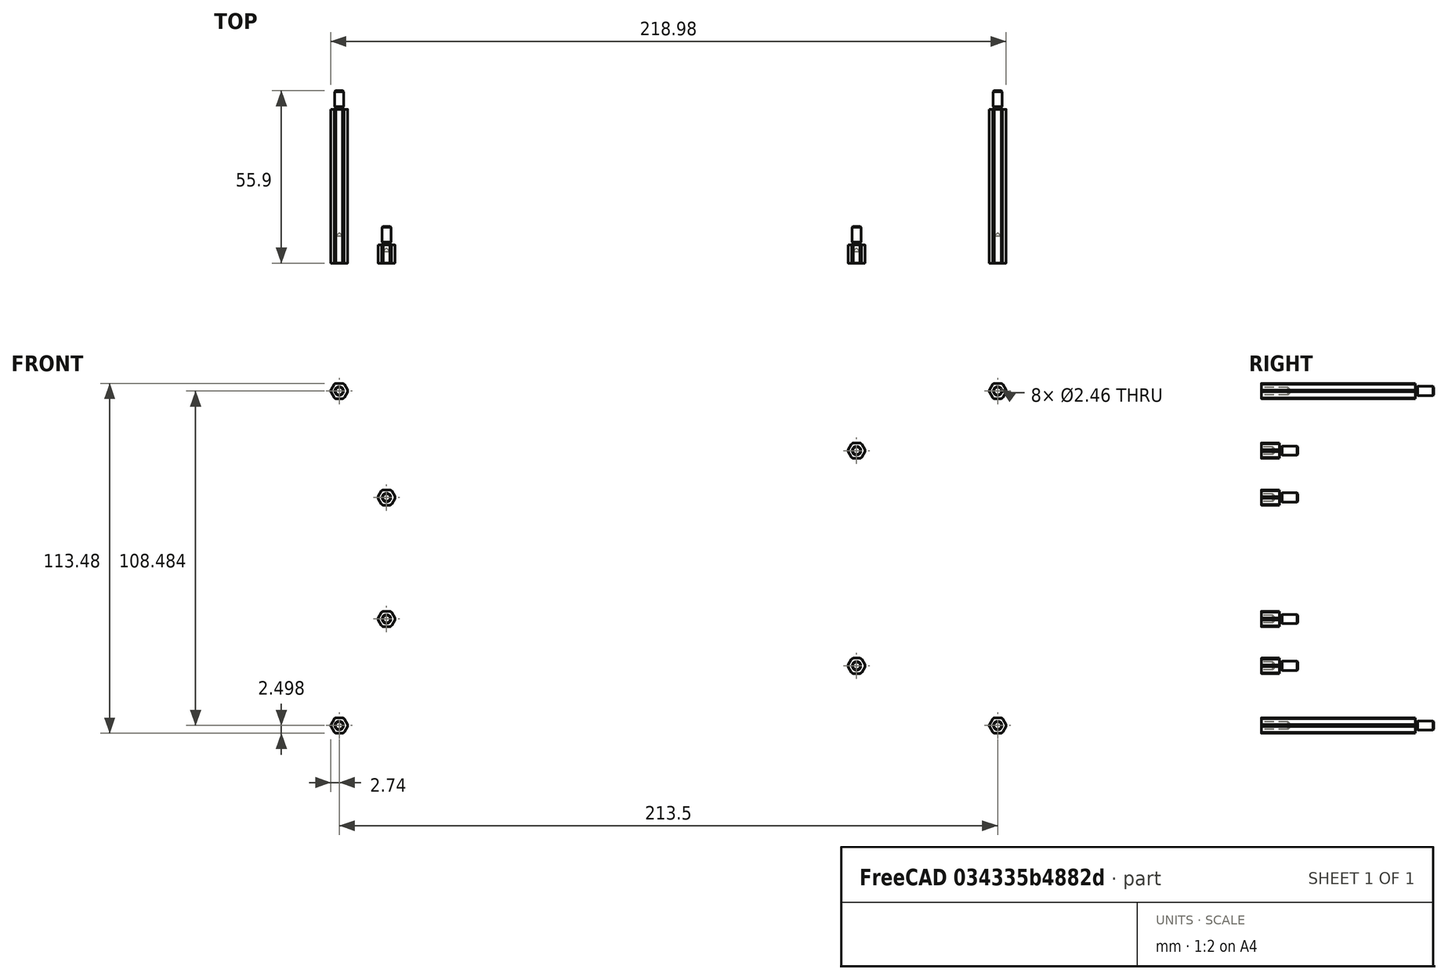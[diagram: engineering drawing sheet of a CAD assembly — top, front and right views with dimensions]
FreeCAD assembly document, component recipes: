
FREECAD ASSEMBLY — COMPONENT RECIPES ("psu")

This assembly document has 8 components, labeled P0..P7 below (a component is one placed body or linked part). 7 of them carry a construction recipe — the FreeCAD feature program that regenerates the part from scratch, quoted from this document or its linked companion documents; the rest are supplied as boundary geometry only. No exploded tour is included for this assembly.
COMPONENT P0 — recipe-attached ("PowerEntry", a linked part whose construction recipe lives in a companion FreeCAD document of the same project; that document's serialized recipe follows).
Construction recipe (the companion document, serialized — sketch geometry with constraints, then the solid features built on it; lengths are millimeters unless a unit is written):

FCSTD DOCUMENT  (FreeCAD 1.0R38641 +468 (Git))
Label: qualtek_power_entry
License: All rights reserved
LicenseURL: https://en.wikipedia.org/wiki/All_rights_reserved
objects: Sketcher::SketchObject×2, PartDesign::Pad×1, PartDesign::Pocket×1, PartDesign::Body×1
note: 11 computed .brp shape members not serialized (recipe doc carries the construction recipe); baked Part::Feature solids carry a one-line shape summary decoded from their .brp

FEATURE [Sketcher::SketchObject] Sketch001
  ArcFitTolerance = 1e-06
  FullyConstrained = false
  MakeInternals = false
  MapMode = 5
  Placement = pos=(0,0,0) rot=(0.57735,0.57735,0.57735;2.0944rad)
  sketch-geometry (17):
    g0: LineSegment StartX=39 StartY=9.70127 StartZ=0 EndX=39 EndY=40.2987 EndZ=0
    g1: LineSegment StartX=-39 StartY=40.2987 StartZ=0 EndX=-39 EndY=9.70127 EndZ=0
    g2: LineSegment StartX=36.545 StartY=43.2488 StartZ=0 EndX=0 EndY=50 EndZ=0
    g3: LineSegment StartX=0 StartY=50 StartZ=0 EndX=-36.545 EndY=43.2488 EndZ=0
    g4: LineSegment StartX=-36.545 StartY=6.75119 StartZ=0 EndX=0 EndY=0 EndZ=0
    g5: LineSegment StartX=0 StartY=0 StartZ=0 EndX=36.545 EndY=6.75119 EndZ=0
    g6: ArcOfCircle CenterX=-36 CenterY=40.2987 CenterZ=0 NormalX=0 NormalY=0 NormalZ=1 AngleXU=0 Radius=3 StartAngle=1.75347 EndAngle=3.14159
    g7: GeomPoint [constr] X=-39 Y=42.7953 Z=0
    g8: ArcOfCircle CenterX=36 CenterY=40.2987 CenterZ=0 NormalX=0 NormalY=0 NormalZ=1 AngleXU=0 Radius=3 StartAngle=7e-16 EndAngle=1.38812
    g9: GeomPoint [constr] X=39 Y=42.7953 Z=0
    g10: ArcOfCircle CenterX=36 CenterY=9.70127 CenterZ=0 NormalX=0 NormalY=0 NormalZ=1 AngleXU=0 Radius=3 StartAngle=4.89507 EndAngle=6.28319
    g11: GeomPoint [constr] X=39 Y=7.20472 Z=0
    g12: ArcOfCircle CenterX=-36 CenterY=9.70127 CenterZ=0 NormalX=0 NormalY=0 NormalZ=1 AngleXU=0 Radius=3 StartAngle=3.14159 EndAngle=4.52971
    g13: GeomPoint [constr] X=-39 Y=7.20472 Z=0
    g14: LineSegment [constr] StartX=-39 StartY=25 StartZ=0 EndX=39 EndY=25 EndZ=0
    g15: LineSegment [constr] StartX=0 StartY=50 StartZ=0 EndX=2.5e-15 EndY=25 EndZ=0
    g16: LineSegment [constr] StartX=2.5e-15 StartY=25 StartZ=0 EndX=0 EndY=0 EndZ=0
  constraints (38):
    c: Vertical(g0)
    c: Vertical(g1)
    c: Coincident(g2,g3)
    c: Coincident(g4,g5)
    c: DistanceY(g4,g2) = 50
    c: DistanceX(g13,g11) = 78
    c: PointOnObject(g7,g1)
    c: PointOnObject(g7,g3)
    c: Tangent(g1,g6) = -1.5708
    c: Tangent(g3,g6) = -1.5708
    c: PointOnObject(g9,g0)
    c: PointOnObject(g9,g2)
    c: Tangent(g0,g8) = -1.5708
    c: Tangent(g2,g8) = -1.5708
    c: PointOnObject(g11,g0)
    c: PointOnObject(g11,g5)
    c: Tangent(g0,g10) = -1.5708
    c: Tangent(g5,g10) = -1.5708
    c: PointOnObject(g13,g1)
    c: PointOnObject(g13,g4)
    c: Tangent(g1,g12) = -1.5708
    c: Tangent(g4,g12) = -1.5708
    c: Equal(g12,g6)
    c: Equal(g6,g8)
    c: Equal(g8,g10)
    c: Radius(g6) = 3
    c: Equal(g3,g2)
    c: Coincident(g4,g-1)
    c: Equal(g0,g1)
    c: Equal(g5,g4)
    c: PointOnObject(g2,g-2)
    c: Symmetric(g1,g1,g14)
    c: Symmetric(g0,g0,g14)
    c: Coincident(g15,g2)
    c: Symmetric(g14,g14,g15)
    c: Coincident(g16,g15)
    c: Coincident(g16,g4)
    c: Equal(g16,g15)
FEATURE [Sketcher::SketchObject] Sketch
  ArcFitTolerance = 1e-06
  AttachmentSupport = -> [YZ_Plane]
  ExternalGeometry = -> [Sketch001]
  FullyConstrained = true
  MakeInternals = false
  MapMode = 5
  Placement = pos=(0,0,0) rot=(0.57735,0.57735,0.57735;2.0944rad)
  sketch-geometry (18):
    g0: LineSegment StartX=-33.75 StartY=10.95 StartZ=0 EndX=33.75 EndY=10.95 EndZ=0
    g1: LineSegment StartX=36.25 StartY=13.45 StartZ=0 EndX=36.25 EndY=36.55 EndZ=0
    g2: LineSegment StartX=33.75 StartY=39.05 StartZ=0 EndX=-33.75 EndY=39.05 EndZ=0
    g3: LineSegment StartX=-36.25 StartY=36.55 StartZ=0 EndX=-36.25 EndY=13.45 EndZ=0
    g4: Circle CenterX=0 CenterY=45 CenterZ=0 NormalX=0 NormalY=0 NormalZ=1 AngleXU=0 Radius=1.75
    g5: Circle CenterX=-1.13e-14 CenterY=5 CenterZ=0 NormalX=0 NormalY=0 NormalZ=1 AngleXU=0 Radius=1.75
    g6: ArcOfCircle CenterX=-33.75 CenterY=36.55 CenterZ=0 NormalX=0 NormalY=0 NormalZ=1 AngleXU=0 Radius=2.5 StartAngle=1.5708 EndAngle=3.14159
    g7: GeomPoint [constr] X=-36.25 Y=39.05 Z=0
    g8: ArcOfCircle CenterX=-33.75 CenterY=13.45 CenterZ=0 NormalX=0 NormalY=0 NormalZ=1 AngleXU=0 Radius=2.5 StartAngle=3.14159 EndAngle=4.71239
    g9: GeomPoint [constr] X=-36.25 Y=10.95 Z=0
    g10: ArcOfCircle CenterX=33.75 CenterY=13.45 CenterZ=0 NormalX=0 NormalY=0 NormalZ=1 AngleXU=0 Radius=2.5 StartAngle=4.71239 EndAngle=6.28319
    g11: GeomPoint [constr] X=36.25 Y=10.95 Z=0
    g12: ArcOfCircle CenterX=33.75 CenterY=36.55 CenterZ=0 NormalX=0 NormalY=0 NormalZ=1 AngleXU=0 Radius=2.5 StartAngle=8e-16 EndAngle=1.5708
    g13: GeomPoint [constr] X=36.25 Y=39.05 Z=0
    g14: LineSegment [constr] StartX=0 StartY=45 StartZ=0 EndX=0 EndY=39.05 EndZ=0
    g15: LineSegment [constr] StartX=-1.13e-14 StartY=5 StartZ=0 EndX=-1.13e-14 EndY=10.95 EndZ=0
    g16: LineSegment [constr] StartX=0 StartY=50 StartZ=0 EndX=0 EndY=45 EndZ=0
    g17: LineSegment [constr] StartX=-1.13e-14 StartY=5 StartZ=0 EndX=0 EndY=0 EndZ=0
  constraints (42):
    c: Horizontal(g0)
    c: Horizontal(g2)
    c: Vertical(g1)
    c: Vertical(g3)
    c: Diameter(g4) = 3.5
    c: DistanceY(g5,g4) = 40
    c: DistanceY(g11,g13) = 28.1
    c: DistanceX(g9,g11) = 72.5
    c: PointOnObject(g7,g2)
    c: PointOnObject(g7,g3)
    c: Tangent(g2,g6) = -1.5708
    c: Tangent(g3,g6) = -1.5708
    c: PointOnObject(g9,g0)
    c: PointOnObject(g9,g3)
    c: Tangent(g0,g8) = -1.5708
    c: Tangent(g3,g8) = -1.5708
    c: PointOnObject(g11,g0)
    c: PointOnObject(g11,g1)
    c: Tangent(g0,g10) = -1.5708
    c: Tangent(g1,g10) = -1.5708
    c: PointOnObject(g13,g1)
    c: PointOnObject(g13,g2)
    c: Tangent(g1,g12) = -1.5708
    c: Tangent(g2,g12) = -1.5708
    c: Equal(g8,g6)
    c: Equal(g12,g10)
    c: Equal(g8,g10)
    c: Radius(g8) = 2.5
    c: Coincident(g14,g4)
    c: Symmetric(g2,g2,g14)
    c: Vertical(g14)
    c: Coincident(g15,g5)
    c: Symmetric(g0,g0,g15)
    c: Vertical(g15)
    c: Equal(g15,g14)
    c: Equal(g5,g4)
    c: Coincident(g16,g-3)
    c: Coincident(g16,g4)
    c: Vertical(g16)
    c: Coincident(g17,g5)
    c: Coincident(g17,g-1)
    c: Equal(g17,g16)
FEATURE [PartDesign::Pad] Pad
  Direction = (1,0,0)
  Length = 5
  Length2 = 10
  Placement = pos=(0,0,0) rot=(0.57735,0.57735,0.57735;2.0944rad)
  Profile = -> Sketch001
  ReferenceAxis = -> Sketch001 [N_Axis]
  Refine = true
  Suppressed = false
  Type = 0
FEATURE [PartDesign::Pocket] Pocket
  BaseFeature = -> Pad
  Direction = (-1,0,0)
  Length = 0
  Length2 = 5
  Placement = pos=(0,0,0) rot=(0.57735,0.57735,0.57735;2.0944rad)
  Profile = -> Sketch
  ReferenceAxis = -> Sketch [N_Axis]
  Refine = true
  Suppressed = false
  Type = 3
  UpToFace = -> Pad [Face12]
FEATURE [PartDesign::Body] Body  label="PowerEntry"
  AllowCompound = false
  Group = -> [Sketch001,Pad,Sketch,Pocket]
  Origin = -> Origin
  Tip = -> Pocket
COMPONENT P1 — geometry summary ("Psu"; no construction recipe available for this part):
  bounding box: 201.0 x 80.0 x 1.0 mm
  tessellated surface: 1,724 triangles
  volume: 16052 mm^3 (100% of its bounding box)
  symmetry: 2-fold rotationally symmetric about the x axis; mirror-symmetric across its y mid-plane, z mid-plane
COMPONENT P2 — recipe-attached ("PsuSideLong", a linked part whose construction recipe lives in a companion FreeCAD document of the same project; that document's serialized recipe follows).
Construction recipe (the companion document, serialized — sketch geometry with constraints, then the solid features built on it; lengths are millimeters unless a unit is written):

FCSTD DOCUMENT  (FreeCAD 1.0R38641 +468 (Git))
Label: psu_side_long
License: All rights reserved
LicenseURL: https://en.wikipedia.org/wiki/All_rights_reserved
objects: PartDesign::SubShapeBinder×2, Sketcher::SketchObject×1, PartDesign::Pad×1, PartDesign::Body×1
note: 8 computed .brp shape members not serialized (recipe doc carries the construction recipe); baked Part::Feature solids carry a one-line shape summary decoded from their .brp
EXTERNAL_REF file=../dimensions.FCStd obj=VarSet
EXTERNAL_REF file=psu_side_short.FCStd obj=Body
EXTERNAL_REF file=psu_top_and_bottom.FCStd obj=Body

FEATURE [PartDesign::SubShapeBinder] Binder  label="PsuSideShortBinderBinder"
  BindCopyOnChange = 0
  BindMode = 0
  ClaimChildren = false
  Context = -> Body [Binder.]
  Fuse = false
  MakeFace = true
  OffsetFill = false
  OffsetIntersection = false
  OffsetJoinType = 0
  OffsetOpenResult = false
  PartialLoad = false
  Placement = pos=(0.127,0,0) rot=(0,0,1;0rad)
  Refine = true
  Relative = true
  Support = -> [<external psu_side_short.FCStd>#Body]
  _Version = 2
  expr: .Placement.Base.x = dimensions#VarSet.EnclosureFinishThickness
FEATURE [PartDesign::SubShapeBinder] Binder001  label="PsuTopAndBottomBinder"
  BindCopyOnChange = 0
  BindMode = 0
  ClaimChildren = false
  Context = -> Body [Binder001.]
  Fuse = false
  MakeFace = true
  OffsetFill = false
  OffsetIntersection = false
  OffsetJoinType = 0
  OffsetOpenResult = false
  PartialLoad = false
  Refine = true
  Relative = true
  Support = -> [<external psu_top_and_bottom.FCStd>#Body]
  _Version = 2
FEATURE [Sketcher::SketchObject] Sketch
  ArcFitTolerance = 1e-06
  AttachmentSupport = -> [Binder001]
  ExternalGeometry = -> [Binder001,Binder]
  FullyConstrained = true
  MakeInternals = false
  MapMode = 5
  Placement = pos=(0,-3.1e-15,-14.1418) rot=(0,0,1;0rad)
  expr: Constraints[183] = dimensions#VarSet.EnclosureCornerRadius
  expr: Constraints[49] = dimensions#VarSet.EnclosureFinishThickness
  sketch-geometry (113):
    g0: LineSegment [constr] StartX=303.647 StartY=129.081 StartZ=0 EndX=303.52 EndY=129.081 EndZ=0
    g1: LineSegment [constr] StartX=240.305 StartY=129.081 StartZ=0 EndX=240.178 EndY=129.081 EndZ=0
    g2: LineSegment [constr] StartX=123.353 StartY=129.081 StartZ=0 EndX=123.48 EndY=129.081 EndZ=0
    g3: LineSegment [constr] StartX=186.695 StartY=129.081 StartZ=0 EndX=186.568 EndY=129.081 EndZ=0
    g4: LineSegment [constr] StartX=326.235 StartY=133.444 StartZ=0 EndX=326.235 EndY=133.571 EndZ=0
    g5: LineSegment [constr] StartX=326.235 StartY=174.719 StartZ=0 EndX=326.235 EndY=174.592 EndZ=0
    g6: LineSegment StartX=326.235 StartY=174.592 StartZ=0 EndX=328.089 EndY=174.592 EndZ=0
    g7: LineSegment StartX=329.289 StartY=173.392 StartZ=0 EndX=329.289 EndY=134.771 EndZ=0
    g8: LineSegment StartX=328.089 StartY=133.571 StartZ=0 EndX=326.235 EndY=133.571 EndZ=0
    g9: LineSegment StartX=303.52 StartY=129.081 StartZ=0 EndX=303.52 EndY=127.227 EndZ=0
    g10: LineSegment StartX=240.178 StartY=129.081 StartZ=0 EndX=240.178 EndY=127.227 EndZ=0
    g11: LineSegment StartX=241.378 StartY=126.027 StartZ=0 EndX=302.32 EndY=126.027 EndZ=0
    g12: LineSegment StartX=186.568 StartY=129.081 StartZ=0 EndX=186.568 EndY=127.227 EndZ=0
    g13: LineSegment StartX=123.48 StartY=129.081 StartZ=0 EndX=123.48 EndY=127.227 EndZ=0
    g14: LineSegment StartX=124.68 StartY=126.027 StartZ=0 EndX=185.368 EndY=126.027 EndZ=0
    g15: LineSegment StartX=240.178 StartY=179.081 StartZ=0 EndX=240.178 EndY=180.935 EndZ=0
    g16: LineSegment StartX=241.378 StartY=182.135 StartZ=0 EndX=302.32 EndY=182.135 EndZ=0
    g17: LineSegment StartX=303.52 StartY=180.935 StartZ=0 EndX=303.52 EndY=179.081 EndZ=0
    g18: LineSegment StartX=304.72 StartY=130.281 StartZ=0 EndX=323.835 EndY=130.281 EndZ=0
    g19: LineSegment StartX=325.035 StartY=131.481 StartZ=0 EndX=325.035 EndY=132.371 EndZ=0
    g20: LineSegment StartX=304.72 StartY=177.881 StartZ=0 EndX=323.835 EndY=177.881 EndZ=0
    g21: LineSegment StartX=325.035 StartY=176.681 StartZ=0 EndX=325.035 EndY=175.792 EndZ=0
    g22: LineSegment StartX=187.768 StartY=130.281 StartZ=0 EndX=238.978 EndY=130.281 EndZ=0
    g23: LineSegment StartX=122.28 StartY=130.281 StartZ=0 EndX=103.165 EndY=130.281 EndZ=0
    g24: LineSegment StartX=101.965 StartY=131.481 StartZ=0 EndX=101.965 EndY=132.371 EndZ=0
    g25: LineSegment StartX=100.765 StartY=133.571 StartZ=0 EndX=98.9106 EndY=133.571 EndZ=0
    g26: LineSegment StartX=97.7106 StartY=134.771 StartZ=0 EndX=97.7106 EndY=173.392 EndZ=0
    g27: LineSegment StartX=98.9106 StartY=174.592 StartZ=0 EndX=100.765 EndY=174.592 EndZ=0
    g28: LineSegment StartX=101.965 StartY=175.792 StartZ=0 EndX=101.965 EndY=176.681 EndZ=0
    g29: LineSegment StartX=103.165 StartY=177.881 StartZ=0 EndX=122.28 EndY=177.881 EndZ=0
    g30: LineSegment StartX=123.48 StartY=179.081 StartZ=0 EndX=123.48 EndY=180.935 EndZ=0
    g31: LineSegment StartX=124.68 StartY=182.135 StartZ=0 EndX=185.368 EndY=182.135 EndZ=0
    g32: LineSegment StartX=186.568 StartY=180.935 StartZ=0 EndX=186.568 EndY=179.081 EndZ=0
    g33: LineSegment StartX=238.978 StartY=177.881 StartZ=0 EndX=187.768 EndY=177.881 EndZ=0
    g34: ArcOfCircle CenterX=122.28 CenterY=129.081 CenterZ=0 NormalX=0 NormalY=0 NormalZ=1 AngleXU=0 Radius=1.2 StartAngle=4.2e-15 EndAngle=1.5708
    g35: ArcOfCircle CenterX=187.768 CenterY=129.081 CenterZ=0 NormalX=0 NormalY=0 NormalZ=1 AngleXU=0 Radius=1.2 StartAngle=1.5708 EndAngle=3.14159
    g36: ArcOfCircle CenterX=238.978 CenterY=129.081 CenterZ=0 NormalX=0 NormalY=0 NormalZ=1 AngleXU=0 Radius=1.2 StartAngle=2.7e-15 EndAngle=1.5708
    g37: ArcOfCircle CenterX=304.72 CenterY=129.081 CenterZ=0 NormalX=0 NormalY=0 NormalZ=1 AngleXU=0 Radius=1.2 StartAngle=1.5708 EndAngle=3.14159
    g38: ArcOfCircle CenterX=326.235 CenterY=132.371 CenterZ=0 NormalX=0 NormalY=0 NormalZ=1 AngleXU=0 Radius=1.2 StartAngle=1.5708 EndAngle=3.14159
    g39: ArcOfCircle CenterX=326.235 CenterY=175.792 CenterZ=0 NormalX=0 NormalY=0 NormalZ=1 AngleXU=0 Radius=1.2 StartAngle=3.14159 EndAngle=4.71239
    g40: ArcOfCircle CenterX=328.089 CenterY=134.771 CenterZ=0 NormalX=0 NormalY=0 NormalZ=1 AngleXU=0 Radius=1.2 StartAngle=4.71239 EndAngle=6.28319
    g41: GeomPoint [constr] X=329.289 Y=133.571 Z=0
    g42: ArcOfCircle CenterX=328.089 CenterY=173.392 CenterZ=0 NormalX=0 NormalY=0 NormalZ=1 AngleXU=0 Radius=1.2 StartAngle=1.01e-14 EndAngle=1.5708
    g43: GeomPoint [constr] X=329.289 Y=174.592 Z=0
    g44: ArcOfCircle CenterX=323.835 CenterY=176.681 CenterZ=0 NormalX=0 NormalY=0 NormalZ=1 AngleXU=0 Radius=1.2 StartAngle=1.12e-14 EndAngle=1.5708
    g45: GeomPoint [constr] X=325.035 Y=177.881 Z=0
    g46: ArcOfCircle CenterX=304.72 CenterY=179.081 CenterZ=0 NormalX=0 NormalY=0 NormalZ=1 AngleXU=0 Radius=1.2 StartAngle=3.14159 EndAngle=4.71239
    g47: GeomPoint [constr] X=303.52 Y=177.881 Z=0
    g48: ArcOfCircle CenterX=302.32 CenterY=180.935 CenterZ=0 NormalX=0 NormalY=0 NormalZ=1 AngleXU=0 Radius=1.2 StartAngle=6.9e-15 EndAngle=1.5708
    g49: GeomPoint [constr] X=303.52 Y=182.135 Z=0
    g50: ArcOfCircle CenterX=241.378 CenterY=180.935 CenterZ=0 NormalX=0 NormalY=0 NormalZ=1 AngleXU=0 Radius=1.2 StartAngle=1.5708 EndAngle=3.14159
    g51: GeomPoint [constr] X=240.178 Y=182.135 Z=0
    g52: ArcOfCircle CenterX=238.978 CenterY=179.081 CenterZ=0 NormalX=0 NormalY=0 NormalZ=1 AngleXU=0 Radius=1.2 StartAngle=4.71239 EndAngle=6.28319
    g53: GeomPoint [constr] X=240.178 Y=177.881 Z=0
    g54: ArcOfCircle CenterX=187.768 CenterY=179.081 CenterZ=0 NormalX=0 NormalY=0 NormalZ=1 AngleXU=0 Radius=1.2 StartAngle=3.14159 EndAngle=4.71239
    g55: GeomPoint [constr] X=186.568 Y=177.881 Z=0
    g56: ArcOfCircle CenterX=185.368 CenterY=180.935 CenterZ=0 NormalX=0 NormalY=0 NormalZ=1 AngleXU=0 Radius=1.2 StartAngle=-1.07e-14 EndAngle=1.5708
    g57: GeomPoint [constr] X=186.568 Y=182.135 Z=0
    g58: ArcOfCircle CenterX=124.68 CenterY=180.935 CenterZ=0 NormalX=0 NormalY=0 NormalZ=1 AngleXU=0 Radius=1.2 StartAngle=1.5708 EndAngle=3.14159
    g59: GeomPoint [constr] X=123.48 Y=182.135 Z=0
    g60: ArcOfCircle CenterX=122.28 CenterY=179.081 CenterZ=0 NormalX=0 NormalY=0 NormalZ=1 AngleXU=0 Radius=1.2 StartAngle=4.71239 EndAngle=6.28319
    g61: GeomPoint [constr] X=123.48 Y=177.881 Z=0
    g62: ArcOfCircle CenterX=103.165 CenterY=176.681 CenterZ=0 NormalX=0 NormalY=0 NormalZ=1 AngleXU=0 Radius=1.2 StartAngle=1.5708 EndAngle=3.14159
    g63: GeomPoint [constr] X=101.965 Y=177.881 Z=0
    g64: ArcOfCircle CenterX=100.765 CenterY=175.792 CenterZ=0 NormalX=0 NormalY=0 NormalZ=1 AngleXU=0 Radius=1.2 StartAngle=4.71239 EndAngle=6.28319
    g65: GeomPoint [constr] X=101.965 Y=174.592 Z=0
    g66: ArcOfCircle CenterX=98.9106 CenterY=173.392 CenterZ=0 NormalX=0 NormalY=0 NormalZ=1 AngleXU=0 Radius=1.2 StartAngle=1.5708 EndAngle=3.14159
    g67: GeomPoint [constr] X=97.7106 Y=174.592 Z=0
    g68: ArcOfCircle CenterX=98.9106 CenterY=134.771 CenterZ=0 NormalX=0 NormalY=0 NormalZ=1 AngleXU=0 Radius=1.2 StartAngle=3.14159 EndAngle=4.71239
    g69: GeomPoint [constr] X=97.7106 Y=133.571 Z=0
    g70: ArcOfCircle CenterX=100.765 CenterY=132.371 CenterZ=0 NormalX=0 NormalY=0 NormalZ=1 AngleXU=0 Radius=1.2 StartAngle=-8e-15 EndAngle=1.5708
    g71: GeomPoint [constr] X=101.965 Y=133.571 Z=0
    g72: ArcOfCircle CenterX=103.165 CenterY=131.481 CenterZ=0 NormalX=0 NormalY=0 NormalZ=1 AngleXU=0 Radius=1.2 StartAngle=3.14159 EndAngle=4.71239
    g73: GeomPoint [constr] X=101.965 Y=130.281 Z=0
    g74: ArcOfCircle CenterX=124.68 CenterY=127.227 CenterZ=0 NormalX=0 NormalY=0 NormalZ=1 AngleXU=0 Radius=1.2 StartAngle=3.14159 EndAngle=4.71239
    g75: GeomPoint [constr] X=123.48 Y=126.027 Z=0
    g76: ArcOfCircle CenterX=185.368 CenterY=127.227 CenterZ=0 NormalX=0 NormalY=0 NormalZ=1 AngleXU=0 Radius=1.2 StartAngle=4.71239 EndAngle=6.28319
    g77: GeomPoint [constr] X=186.568 Y=126.027 Z=0
    g78: ArcOfCircle CenterX=241.378 CenterY=127.227 CenterZ=0 NormalX=0 NormalY=0 NormalZ=1 AngleXU=0 Radius=1.2 StartAngle=3.14159 EndAngle=4.71239
    g79: GeomPoint [constr] X=240.178 Y=126.027 Z=0
    g80: ArcOfCircle CenterX=302.32 CenterY=127.227 CenterZ=0 NormalX=0 NormalY=0 NormalZ=1 AngleXU=0 Radius=1.2 StartAngle=4.71239 EndAngle=6.28319
    g81: GeomPoint [constr] X=303.52 Y=126.027 Z=0
    g82: ArcOfCircle CenterX=323.835 CenterY=131.481 CenterZ=0 NormalX=0 NormalY=0 NormalZ=1 AngleXU=0 Radius=1.2 StartAngle=4.71239 EndAngle=6.28319
    g83: GeomPoint [constr] X=325.035 Y=130.281 Z=0
    g84: LineSegment [constr] StartX=120.6 StartY=129.081 StartZ=0 EndX=120.6 EndY=126.027 EndZ=0
    g85: LineSegment [constr] StartX=120.6 StartY=126.027 StartZ=0 EndX=124.68 EndY=126.027 EndZ=0
    g86: LineSegment [constr] StartX=185.368 StartY=126.027 StartZ=0 EndX=189.448 EndY=126.027 EndZ=0
    g87: LineSegment [constr] StartX=189.448 StartY=126.027 StartZ=0 EndX=189.448 EndY=139.081 EndZ=0
    g88: LineSegment [constr] StartX=120.6 StartY=129.081 StartZ=0 EndX=120.6 EndY=139.081 EndZ=0
    g89: ArcOfCircle CenterX=120.6 CenterY=141.224 CenterZ=0 NormalX=0 NormalY=0 NormalZ=1 AngleXU=0 Radius=2.14286 StartAngle=1.5708 EndAngle=4.71239
    g90: ArcOfCircle CenterX=189.448 CenterY=141.224 CenterZ=0 NormalX=0 NormalY=0 NormalZ=1 AngleXU=0 Radius=2.14286 StartAngle=4.71239 EndAngle=7.85398
    g91: LineSegment StartX=120.6 StartY=143.367 StartZ=0 EndX=189.448 EndY=143.367 EndZ=0
    g92: LineSegment StartX=120.6 StartY=139.081 StartZ=0 EndX=189.448 EndY=139.081 EndZ=0
    g93: ArcOfCircle CenterX=120.6 CenterY=149.796 CenterZ=0 NormalX=0 NormalY=0 NormalZ=1 AngleXU=0 Radius=2.14286 StartAngle=1.5708 EndAngle=4.71239
    g94: ArcOfCircle CenterX=189.448 CenterY=149.796 CenterZ=0 NormalX=0 NormalY=0 NormalZ=1 AngleXU=0 Radius=2.14286 StartAngle=4.71239 EndAngle=7.85398
    g95: LineSegment StartX=120.6 StartY=151.938 StartZ=0 EndX=189.448 EndY=151.938 EndZ=0
    g96: LineSegment StartX=120.6 StartY=147.653 StartZ=0 EndX=189.448 EndY=147.653 EndZ=0
    g97: LineSegment [constr] StartX=120.6 StartY=139.081 StartZ=0 EndX=120.6 EndY=143.367 EndZ=0
    g98: LineSegment [constr] StartX=120.6 StartY=143.367 StartZ=0 EndX=120.6 EndY=147.653 EndZ=0
    g99: LineSegment [constr] StartX=120.6 StartY=147.653 StartZ=0 EndX=120.6 EndY=151.938 EndZ=0
    g100: LineSegment [constr] StartX=120.6 StartY=151.938 StartZ=0 EndX=120.6 EndY=156.224 EndZ=0
    g101: LineSegment [constr] StartX=120.6 StartY=156.224 StartZ=0 EndX=120.6 EndY=160.51 EndZ=0
    g102: LineSegment [constr] StartX=120.6 StartY=160.51 StartZ=0 EndX=120.6 EndY=164.796 EndZ=0
    g103: LineSegment [constr] StartX=120.6 StartY=164.796 StartZ=0 EndX=120.6 EndY=169.081 EndZ=0
    g104: ArcOfCircle CenterX=120.6 CenterY=158.367 CenterZ=0 NormalX=0 NormalY=0 NormalZ=1 AngleXU=0 Radius=2.14286 StartAngle=1.5708 EndAngle=4.71239
    g105: ArcOfCircle CenterX=189.448 CenterY=158.367 CenterZ=0 NormalX=0 NormalY=0 NormalZ=1 AngleXU=0 Radius=2.14286 StartAngle=4.71239 EndAngle=7.85398
    g106: LineSegment StartX=120.6 StartY=160.51 StartZ=0 EndX=189.448 EndY=160.51 EndZ=0
    g107: LineSegment StartX=120.6 StartY=156.224 StartZ=0 EndX=189.448 EndY=156.224 EndZ=0
    g108: ArcOfCircle CenterX=120.6 CenterY=166.938 CenterZ=0 NormalX=0 NormalY=0 NormalZ=1 AngleXU=0 Radius=2.14286 StartAngle=1.5708 EndAngle=4.71239
    g109: ArcOfCircle CenterX=189.448 CenterY=166.938 CenterZ=0 NormalX=0 NormalY=0 NormalZ=1 AngleXU=0 Radius=2.14286 StartAngle=4.71239 EndAngle=7.85398
    g110: LineSegment StartX=120.6 StartY=169.081 StartZ=0 EndX=189.448 EndY=169.081 EndZ=0
    g111: LineSegment StartX=120.6 StartY=164.796 StartZ=0 EndX=189.448 EndY=164.796 EndZ=0
    g112: LineSegment [constr] StartX=189.448 StartY=139.081 StartZ=0 EndX=189.448 EndY=169.081 EndZ=0
  constraints (266):
    c: Coincident(g0,g-4)
    c: PointOnObject(g0,g-4)
    c: Coincident(g1,g-4)
    c: Coincident(g2,g-3)
    c: Coincident(g3,g-3)
    c: Coincident(g4,g-5)
    c: PointOnObject(g4,g-5)
    c: Coincident(g5,g-5)
    c: PointOnObject(g5,g-5)
    c: Equal(g4,g5)
    c: Equal(g0,g4)
    c: Equal(g0,g1)
    c: Equal(g1,g3)
    c: Equal(g3,g2)
    c: Horizontal(g6)
    c: Vertical(g7)
    c: Horizontal(g8)
    c: Vertical(g9)
    c: Horizontal(g11)
    c: Vertical(g13)
    c: Horizontal(g14)
    c: Vertical(g15)
    c: Horizontal(g16)
    c: Vertical(g17)
    c: Horizontal(g18)
    c: Vertical(g19)
    c: Horizontal(g20)
    c: Vertical(g21)
    c: Horizontal(g23)
    c: Vertical(g24)
    c: Horizontal(g25)
    c: Vertical(g26)
    c: Horizontal(g27)
    c: Vertical(g28)
    c: Horizontal(g29)
    c: Vertical(g30)
    c: Horizontal(g31)
    c: Vertical(g32)
    c: Horizontal(g33)
    c: Tangent(g34,g23) = -1.5708
    c: Tangent(g37,g18) = 1.5708
    c: Tangent(g9,g37) = -1.5708
    c: Coincident(g9,g0)
    c: Tangent(g38,g8) = -1.5708
    c: Coincident(g8,g4)
    c: Tangent(g19,g38) = 1.5708
    c: Tangent(g6,g39) = -1.5708
    c: Coincident(g5,g6)
    c: Tangent(g39,g21) = -1.5708
    c: DistanceY(g4,g4) = 0.127
    c: PointOnObject(g41,g7)
    c: PointOnObject(g41,g8)
    c: Tangent(g7,g40) = 1.5708
    c: Tangent(g8,g40) = 1.5708
    c: PointOnObject(g43,g6)
    c: PointOnObject(g43,g7)
    c: Tangent(g6,g42) = 1.5708
    c: Tangent(g7,g42) = 1.5708
    c: PointOnObject(g45,g20)
    c: PointOnObject(g45,g21)
    c: Tangent(g20,g44) = 1.5708
    c: Tangent(g21,g44) = 1.5708
    c: PointOnObject(g47,g17)
    c: PointOnObject(g47,g20)
    c: Tangent(g17,g46) = -1.5708
    c: Tangent(g20,g46) = -1.5708
    c: PointOnObject(g49,g16)
    c: PointOnObject(g49,g17)
    c: Tangent(g16,g48) = 1.5708
    c: Tangent(g17,g48) = 1.5708
    c: PointOnObject(g51,g15)
    c: PointOnObject(g51,g16)
    c: Tangent(g15,g50) = 1.5708
    c: Tangent(g16,g50) = 1.5708
    c: PointOnObject(g53,g15)
    c: PointOnObject(g53,g33)
    c: Tangent(g15,g52) = -1.5708
    c: Tangent(g33,g52) = 1.5708
    c: PointOnObject(g55,g32)
    c: PointOnObject(g55,g33)
    c: Tangent(g32,g54) = -1.5708
    c: Tangent(g33,g54) = 1.5708
    c: PointOnObject(g57,g31)
    c: PointOnObject(g57,g32)
    c: Tangent(g31,g56) = 1.5708
    c: Tangent(g32,g56) = 1.5708
    c: PointOnObject(g59,g30)
    c: PointOnObject(g59,g31)
    c: Tangent(g30,g58) = 1.5708
    c: Tangent(g31,g58) = 1.5708
    c: PointOnObject(g61,g29)
    c: PointOnObject(g61,g30)
    c: Tangent(g29,g60) = -1.5708
    c: Tangent(g30,g60) = -1.5708
    c: PointOnObject(g63,g28)
    c: PointOnObject(g63,g29)
    c: Tangent(g28,g62) = 1.5708
    c: Tangent(g29,g62) = 1.5708
    c: PointOnObject(g65,g27)
    c: PointOnObject(g65,g28)
    c: Tangent(g27,g64) = -1.5708
    c: Tangent(g28,g64) = -1.5708
    c: PointOnObject(g67,g26)
    c: PointOnObject(g67,g27)
    c: Tangent(g26,g66) = 1.5708
    c: Tangent(g27,g66) = 1.5708
    c: PointOnObject(g69,g25)
    c: PointOnObject(g69,g26)
    c: Tangent(g25,g68) = 1.5708
    c: Tangent(g26,g68) = 1.5708
    c: PointOnObject(g71,g24)
    c: PointOnObject(g71,g25)
    c: Tangent(g24,g70) = -1.5708
    c: Tangent(g25,g70) = -1.5708
    c: PointOnObject(g73,g23)
    c: PointOnObject(g73,g24)
    c: Tangent(g23,g72) = 1.5708
    c: Tangent(g24,g72) = 1.5708
    c: PointOnObject(g75,g13)
    c: PointOnObject(g75,g14)
    c: Tangent(g13,g74) = -1.5708
    c: Tangent(g14,g74) = -1.5708
    c: PointOnObject(g77,g12)
    c: PointOnObject(g77,g14)
    c: Tangent(g12,g76) = 1.5708
    c: Tangent(g14,g76) = -1.5708
    c: PointOnObject(g79,g10)
    c: PointOnObject(g79,g11)
    c: Tangent(g10,g78) = -1.5708
    c: Tangent(g11,g78) = -1.5708
    c: PointOnObject(g81,g9)
    c: PointOnObject(g81,g11)
    c: Tangent(g9,g80) = 1.5708
    c: Tangent(g11,g80) = -1.5708
    c: PointOnObject(g83,g18)
    c: PointOnObject(g83,g19)
    c: Tangent(g18,g82) = -1.5708
    c: Tangent(g19,g82) = -1.5708
    c: Equal(g34,g35)
    c: Equal(g36,g37)
    c: Equal(g37,g38)
    c: Equal(g38,g39)
    c: Equal(g39,g40)
    c: Equal(g40,g42)
    c: Equal(g42,g44)
    c: Equal(g44,g46)
    c: Equal(g46,g48)
    c: Equal(g48,g50)
    c: Equal(g50,g52)
    c: Equal(g52,g54)
    c: Equal(g54,g56)
    c: Equal(g56,g58)
    c: Equal(g58,g60)
    c: Equal(g60,g62)
    c: Equal(g62,g64)
    c: Equal(g64,g66)
    c: Equal(g66,g68)
    c: Equal(g68,g70)
    c: Equal(g70,g72)
    c: Equal(g72,g74)
    c: Equal(g74,g76)
    c: Equal(g76,g78)
    c: Equal(g78,g80)
    c: Equal(g80,g82)
    c: Tangent(g35,g12) = -1.5708
    c: Tangent(g35,g22) = 1.5708
    c: Coincident(g12,g3)
    c: PointOnObject(g3,g-3)
    c: PointOnObject(g2,g-3)
    c: PointOnObject(g1,g-4)
    c: Tangent(g36,g10) = 1.5708
    c: Coincident(g10,g1)
    c: Tangent(g36,g22) = 1.5708
    c: Vertical(g10)
    c: Vertical(g12)
    c: Horizontal(g22)
    c: Tangent(g34,g13) = 1.5708
    c: Coincident(g13,g2)
    c: Equal(g31,g14)
    c: Equal(g22,g33)
    c: Equal(g11,g16)
    c: Equal(g18,g20)
    c: Equal(g21,g19)
    c: Radius(g38) = 1.2
    c: Equal(g9,g17)
    c: PointOnObject(g9,g-7)
    c: Equal(g10,g15)
    c: PointOnObject(g12,g-8)
    c: Equal(g12,g32)
    c: Equal(g30,g13)
    c: Equal(g23,g29)
    c: Equal(g24,g19)
    c: Equal(g21,g28)
    c: Equal(g23,g18)
    c: Equal(g27,g6)
    c: PointOnObject(g6,g-6)
    c: Vertical(g84)
    c: Coincident(g85,g84)
    c: Horizontal(g85)
    c: Coincident(g85,g14)
    c: Coincident(g86,g14)
    c: Horizontal(g86)
    c: Coincident(g87,g86)
    c: Vertical(g87)
    c: Equal(g86,g85)
    c: Coincident(g-9,g84)
    c: Coincident(g88,g84)
    c: Vertical(g88)
    c: Tangent(g89,g91) = 1.5708
    c: Tangent(g89,g92) = -1.5708
    c: Tangent(g90,g91) = 1.5708
    c: Tangent(g90,g92) = -1.5708
    c: Equal(g89,g90)
    c: Horizontal(g91)
    c: Tangent(g93,g95) = 1.5708
    c: Tangent(g93,g96) = -1.5708
    c: Tangent(g94,g95) = 1.5708
    c: Tangent(g94,g96) = -1.5708
    c: Equal(g93,g94)
    c: Horizontal(g95)
    c: Coincident(g97,g89)
    c: Coincident(g97,g89)
    c: Coincident(g98,g89)
    c: Coincident(g98,g93)
    c: Coincident(g99,g93)
    c: Coincident(g99,g93)
    c: Coincident(g100,g93)
    c: Vertical(g100)
    c: Equal(g97,g98)
    c: Vertical(g98)
    c: Equal(g99,g98)
    c: Equal(g100,g99)
    c: Vertical(g101)
    c: Coincident(g102,g101)
    c: Vertical(g102)
    c: Coincident(g103,g102)
    c: Vertical(g103)
    c: Coincident(g90,g87)
    c: Tangent(g104,g106) = 1.5708
    c: Tangent(g104,g107) = -1.5708
    c: Tangent(g105,g106) = 1.5708
    c: Tangent(g105,g107) = -1.5708
    c: Coincident(g101,g104)
    c: Coincident(g100,g101)
    c: Coincident(g100,g104)
    c: Horizontal(g106)
    c: Tangent(g108,g110) = 1.5708
    c: Tangent(g108,g111) = -1.5708
    c: Tangent(g109,g110) = 1.5708
    c: Tangent(g109,g111) = -1.5708
    c: Equal(g108,g109)
    c: Equal(g101,g100)
    c: Equal(g102,g101)
    c: Equal(g102,g103)
    c: Coincident(g102,g108)
    c: Coincident(g108,g103)
    c: Coincident(g112,g87)
    c: Vertical(g112)
    c: Coincident(g109,g112)
    c: PointOnObject(g105,g112)
    c: PointOnObject(g94,g112)
    c: Coincident(g88,g89)
    c: DistanceY(g88,g88) = 10
    c: DistanceY(g84,g103) = 40
    c: Distance(g31,g110) = 13.0542
    c: Distance(g14,g92) = 13.0542
FEATURE [PartDesign::Pad] Pad
  Direction = (0,0,1)
  Length = 1.8542
  Length2 = 10
  Profile = -> Sketch
  ReferenceAxis = -> Sketch [N_Axis]
  Refine = true
  Suppressed = false
  Type = 0
  expr: Length = dimensions#VarSet.EnclosureTotalThickness
FEATURE [PartDesign::Body] Body  label="PsuSideLong"
  AllowCompound = false
  Group = -> [Binder,Binder001,Sketch,Pad]
  Origin = -> Origin
  Tip = -> Pad
COMPONENT P3 — same part as P2; its construction recipe is shown at P2.
COMPONENT P4 — recipe-attached ("PsuSideShort", a linked part whose construction recipe lives in a companion FreeCAD document of the same project; that document's serialized recipe follows).
Construction recipe (the companion document, serialized — sketch geometry with constraints, then the solid features built on it; lengths are millimeters unless a unit is written):

FCSTD DOCUMENT  (FreeCAD 1.0R38641 +468 (Git))
Label: psu_side_short
License: All rights reserved
LicenseURL: https://en.wikipedia.org/wiki/All_rights_reserved
objects: PartDesign::SubShapeBinder×2, Sketcher::SketchObject×1, PartDesign::Pad×1, PartDesign::Body×1
note: 8 computed .brp shape members not serialized (recipe doc carries the construction recipe); baked Part::Feature solids carry a one-line shape summary decoded from their .brp
EXTERNAL_REF file=../../third_party/qualtek_power_entry.FCStd obj=Body
EXTERNAL_REF file=psu_top_and_bottom.FCStd obj=Body
EXTERNAL_REF file=../dimensions.FCStd obj=VarSet

FEATURE [PartDesign::SubShapeBinder] Binder  label="PowerEntryBinder"
  BindCopyOnChange = 0
  BindMode = 0
  ClaimChildren = false
  Context = -> Body [Binder.]
  Fuse = false
  MakeFace = true
  OffsetFill = false
  OffsetIntersection = false
  OffsetJoinType = 0
  OffsetOpenResult = false
  PartialLoad = false
  Placement = pos=(0,0,0) rot=(1,0,0;1.5708rad)
  Refine = true
  Relative = true
  Support = -> [<external ../../third_party/qualtek_power_entry.FCStd>#Body]
  _Version = 2
FEATURE [PartDesign::SubShapeBinder] Binder001  label="PsuTopAndBottomBinder"
  BindCopyOnChange = 0
  BindMode = 0
  ClaimChildren = false
  Context = -> Body [Binder001.]
  Fuse = false
  MakeFace = true
  OffsetFill = false
  OffsetIntersection = false
  OffsetJoinType = 0
  OffsetOpenResult = false
  PartialLoad = false
  Refine = true
  Relative = true
  Support = -> [<external psu_top_and_bottom.FCStd>#Body]
  _Version = 2
FEATURE [Sketcher::SketchObject] Sketch
  ArcFitTolerance = 1e-06
  AttachmentSupport = -> [Binder001]
  ExternalGeometry = -> [Binder001,Binder]
  FullyConstrained = true
  MakeInternals = false
  MapMode = 5
  Placement = pos=(326.108,0,0) rot=(0.57735,0.57735,0.57735;2.0944rad)
  expr: Constraints[141] = dimensions#VarSet.EnclosureFinishThickness
  expr: Constraints[165] = dimensions#VarSet.EnclosureTotalThickness + 2 * dimensions#VarSet.EnclosureFinishThickness
  expr: Constraints[2] = dimensions#VarSet.EnclosureFinishThickness
  expr: Constraints[31] = dimensions#VarSet.EnclosureCornerRadius
  expr: Constraints[3] = dimensions#VarSet.EnclosureFinishThickness
  sketch-geometry (76):
    g0: LineSegment [constr] StartX=129.081 StartY=-24.706 StartZ=0 EndX=129.081 EndY=-87.794 EndZ=0
    g1: LineSegment StartX=129.081 StartY=-24.706 StartZ=0 EndX=127.227 EndY=-24.706 EndZ=0
    g2: LineSegment StartX=129.081 StartY=-87.794 StartZ=0 EndX=127.227 EndY=-87.794 EndZ=0
    g3: LineSegment StartX=126.027 StartY=-86.594 StartZ=0 EndX=126.027 EndY=-25.906 EndZ=0
    g4: ArcOfCircle CenterX=129.081 CenterY=-88.994 CenterZ=0 NormalX=0 NormalY=0 NormalZ=1 AngleXU=0 Radius=1.2 StartAngle=-2.7e-15 EndAngle=1.5708
    g5: ArcOfCircle CenterX=129.081 CenterY=-23.506 CenterZ=0 NormalX=0 NormalY=0 NormalZ=1 AngleXU=0 Radius=1.2 StartAngle=4.71239 EndAngle=6.28319
    g6: LineSegment StartX=130.281 StartY=-11.1254 StartZ=0 EndX=130.281 EndY=-23.506 EndZ=0
    g7: LineSegment StartX=130.281 StartY=-88.994 StartZ=0 EndX=130.281 EndY=-101.375 EndZ=0
    g8: LineSegment StartX=131.481 StartY=-102.575 StartZ=0 EndX=176.681 EndY=-102.575 EndZ=0
    g9: LineSegment StartX=131.481 StartY=-9.9254 StartZ=0 EndX=176.681 EndY=-9.9254 EndZ=0
    g10: LineSegment StartX=177.881 StartY=-11.1254 StartZ=0 EndX=177.881 EndY=-23.506 EndZ=0
    g11: LineSegment StartX=179.081 StartY=-24.706 StartZ=0 EndX=180.935 EndY=-24.706 EndZ=0
    g12: LineSegment StartX=182.135 StartY=-25.906 StartZ=0 EndX=182.135 EndY=-86.594 EndZ=0
    g13: LineSegment StartX=180.935 StartY=-87.794 StartZ=0 EndX=179.081 EndY=-87.794 EndZ=0
    g14: LineSegment StartX=177.881 StartY=-88.994 StartZ=0 EndX=177.881 EndY=-101.375 EndZ=0
    g15: ArcOfCircle CenterX=179.081 CenterY=-23.506 CenterZ=0 NormalX=0 NormalY=0 NormalZ=1 AngleXU=0 Radius=1.2 StartAngle=3.14159 EndAngle=4.71239
    g16: GeomPoint [constr] X=177.881 Y=-24.706 Z=0
    g17: ArcOfCircle CenterX=179.081 CenterY=-88.994 CenterZ=0 NormalX=0 NormalY=0 NormalZ=1 AngleXU=0 Radius=1.2 StartAngle=1.5708 EndAngle=3.14159
    g18: ArcOfCircle CenterX=127.227 CenterY=-25.906 CenterZ=0 NormalX=0 NormalY=0 NormalZ=1 AngleXU=0 Radius=1.2 StartAngle=1.5708 EndAngle=3.14159
    g19: GeomPoint [constr] X=126.027 Y=-24.706 Z=0
    g20: ArcOfCircle CenterX=127.227 CenterY=-86.594 CenterZ=0 NormalX=0 NormalY=0 NormalZ=1 AngleXU=0 Radius=1.2 StartAngle=3.14159 EndAngle=4.71239
    g21: GeomPoint [constr] X=126.027 Y=-87.794 Z=0
    g22: ArcOfCircle CenterX=131.481 CenterY=-101.375 CenterZ=0 NormalX=0 NormalY=0 NormalZ=1 AngleXU=0 Radius=1.2 StartAngle=3.14159 EndAngle=4.71239
    g23: GeomPoint [constr] X=130.281 Y=-102.575 Z=0
    g24: ArcOfCircle CenterX=176.681 CenterY=-101.375 CenterZ=0 NormalX=0 NormalY=0 NormalZ=1 AngleXU=0 Radius=1.2 StartAngle=4.71239 EndAngle=6.28319
    g25: GeomPoint [constr] X=177.881 Y=-102.575 Z=0
    g26: ArcOfCircle CenterX=180.935 CenterY=-86.594 CenterZ=0 NormalX=0 NormalY=0 NormalZ=1 AngleXU=0 Radius=1.2 StartAngle=4.71239 EndAngle=6.28319
    g27: GeomPoint [constr] X=182.135 Y=-87.794 Z=0
    g28: ArcOfCircle CenterX=180.935 CenterY=-25.906 CenterZ=0 NormalX=0 NormalY=0 NormalZ=1 AngleXU=0 Radius=1.2 StartAngle=0 EndAngle=1.5708
    g29: GeomPoint [constr] X=182.135 Y=-24.706 Z=0
    g30: ArcOfCircle CenterX=176.681 CenterY=-11.1254 CenterZ=0 NormalX=0 NormalY=0 NormalZ=1 AngleXU=0 Radius=1.2 StartAngle=0 EndAngle=1.5708
    g31: GeomPoint [constr] X=177.881 Y=-9.9254 Z=0
    g32: ArcOfCircle CenterX=131.481 CenterY=-11.1254 CenterZ=0 NormalX=0 NormalY=0 NormalZ=1 AngleXU=0 Radius=1.2 StartAngle=1.5708 EndAngle=3.14159
    g33: GeomPoint [constr] X=130.281 Y=-9.9254 Z=0
    g34: Circle CenterX=134.081 CenterY=-56.25 CenterZ=0 NormalX=0 NormalY=0 NormalZ=1 AngleXU=0 Radius=1.5
    g35: Circle CenterX=174.081 CenterY=-56.25 CenterZ=0 NormalX=0 NormalY=0 NormalZ=1 AngleXU=0 Radius=1.5
    g36: LineSegment [constr] StartX=140.031 StartY=-22.5 StartZ=0 EndX=140.031 EndY=-90 EndZ=0
    g37: LineSegment [constr] StartX=142.531 StartY=-92.5 StartZ=0 EndX=165.631 EndY=-92.5 EndZ=0
    g38: LineSegment [constr] StartX=168.131 StartY=-90 StartZ=0 EndX=168.131 EndY=-22.5 EndZ=0
    g39: LineSegment [constr] StartX=165.631 StartY=-20 StartZ=0 EndX=142.531 EndY=-20 EndZ=0
    g40: ArcOfCircle [constr] CenterX=142.531 CenterY=-22.5 CenterZ=0 NormalX=0 NormalY=0 NormalZ=1 AngleXU=0 Radius=2.5 StartAngle=1.5708 EndAngle=3.14159
    g41: ArcOfCircle [constr] CenterX=142.531 CenterY=-90 CenterZ=0 NormalX=0 NormalY=0 NormalZ=1 AngleXU=0 Radius=2.5 StartAngle=3.14159 EndAngle=4.71239
    g42: ArcOfCircle [constr] CenterX=165.631 CenterY=-90 CenterZ=0 NormalX=0 NormalY=0 NormalZ=1 AngleXU=0 Radius=2.5 StartAngle=4.71239 EndAngle=6.28319
    g43: ArcOfCircle [constr] CenterX=165.631 CenterY=-22.5 CenterZ=0 NormalX=0 NormalY=0 NormalZ=1 AngleXU=0 Radius=2.5 StartAngle=5e-16 EndAngle=1.5708
    g44: GeomPoint [constr] X=140.031 Y=-20 Z=0
    g45: GeomPoint [constr] X=168.131 Y=-92.5 Z=0
    g46: LineSegment [constr] StartX=126.027 StartY=-56.25 StartZ=0 EndX=134.081 EndY=-56.25 EndZ=0
    g47: LineSegment [constr] StartX=134.081 StartY=-56.25 StartZ=0 EndX=140.031 EndY=-56.25 EndZ=0
    g48: LineSegment [constr] StartX=168.131 StartY=-56.25 StartZ=0 EndX=174.081 EndY=-56.25 EndZ=0
    g49: LineSegment [constr] StartX=174.081 StartY=-56.25 StartZ=0 EndX=182.135 EndY=-56.25 EndZ=0
    g50: LineSegment [constr] StartX=-45 StartY=1.4e-14 StartZ=0 EndX=-39.05 EndY=1.31e-14 EndZ=0
    g51: LineSegment [constr] StartX=-10.95 StartY=6.1e-15 StartZ=0 EndX=-5 EndY=-1.07e-14 EndZ=0
    g52: LineSegment StartX=139.904 StartY=-22.5 StartZ=0 EndX=139.904 EndY=-90 EndZ=0
    g53: LineSegment StartX=142.531 StartY=-92.627 StartZ=0 EndX=165.631 EndY=-92.627 EndZ=0
    g54: LineSegment StartX=168.258 StartY=-90 StartZ=0 EndX=168.258 EndY=-22.5 EndZ=0
    g55: LineSegment StartX=165.631 StartY=-19.873 StartZ=0 EndX=142.531 EndY=-19.873 EndZ=0
    g56: ArcOfCircle CenterX=142.531 CenterY=-22.5 CenterZ=0 NormalX=0 NormalY=0 NormalZ=1 AngleXU=0 Radius=2.627 StartAngle=1.5708 EndAngle=3.14159
    g57: ArcOfCircle CenterX=142.531 CenterY=-90 CenterZ=0 NormalX=0 NormalY=0 NormalZ=1 AngleXU=0 Radius=2.627 StartAngle=3.14159 EndAngle=4.71239
    g58: ArcOfCircle CenterX=165.631 CenterY=-90 CenterZ=0 NormalX=0 NormalY=0 NormalZ=1 AngleXU=0 Radius=2.627 StartAngle=4.71239 EndAngle=6.28319
    g59: ArcOfCircle CenterX=165.631 CenterY=-22.5 CenterZ=0 NormalX=0 NormalY=0 NormalZ=1 AngleXU=0 Radius=2.627 StartAngle=5e-16 EndAngle=1.5708
    g60: GeomPoint [constr] X=139.904 Y=-19.873 Z=0
    g61: GeomPoint [constr] X=168.258 Y=-92.627 Z=0
    g62: LineSegment [constr] StartX=-50 StartY=7.1e-15 StartZ=0 EndX=0 EndY=0 EndZ=0
    g63: LineSegment [constr] StartX=129.081 StartY=-87.794 StartZ=0 EndX=179.081 EndY=-87.794 EndZ=0
    g64: ArcOfCircle CenterX=133.444 CenterY=-13.0877 CenterZ=0 NormalX=0 NormalY=0 NormalZ=1 AngleXU=0 Radius=1.0541 StartAngle=1.5708 EndAngle=4.71239
    g65: ArcOfCircle CenterX=174.719 CenterY=-13.0877 CenterZ=0 NormalX=0 NormalY=0 NormalZ=1 AngleXU=0 Radius=1.0541 StartAngle=4.71239 EndAngle=7.85398
    g66: LineSegment StartX=133.444 StartY=-12.0336 StartZ=0 EndX=174.719 EndY=-12.0336 EndZ=0
    g67: LineSegment StartX=133.444 StartY=-14.1418 StartZ=0 EndX=174.719 EndY=-14.1418 EndZ=0
    g68: ArcOfCircle CenterX=133.444 CenterY=-99.4123 CenterZ=0 NormalX=0 NormalY=0 NormalZ=1 AngleXU=0 Radius=1.0541 StartAngle=1.5708 EndAngle=4.71239
    g69: ArcOfCircle CenterX=174.719 CenterY=-99.4123 CenterZ=0 NormalX=0 NormalY=0 NormalZ=1 AngleXU=0 Radius=1.0541 StartAngle=4.71239 EndAngle=7.85398
    g70: LineSegment StartX=133.444 StartY=-98.3582 StartZ=0 EndX=174.719 EndY=-98.3582 EndZ=0
    g71: LineSegment StartX=133.444 StartY=-100.466 StartZ=0 EndX=174.719 EndY=-100.466 EndZ=0
    g72: LineSegment [constr] StartX=154.081 StartY=-102.575 StartZ=0 EndX=154.081 EndY=-100.466 EndZ=0
    g73: LineSegment [constr] StartX=154.081 StartY=-9.9254 StartZ=0 EndX=154.081 EndY=-12.0336 EndZ=0
    g74: LineSegment [constr] StartX=154.081 StartY=-98.3582 StartZ=0 EndX=154.081 EndY=-100.466 EndZ=0
    g75: LineSegment [constr] StartX=130.281 StartY=-99.4123 StartZ=0 EndX=132.389 EndY=-99.4123 EndZ=0
  constraints (177):
    c: PointOnObject(g0,g-3)
    c: PointOnObject(g0,g-3)
    c: DistanceY(g-3,g0) = 0.127
    c: DistanceY(g0,g-3) = 0.127
    c: Horizontal(g1)
    c: Horizontal(g2)
    c: Vertical(g3)
    c: Vertical(g6)
    c: Tangent(g5,g6) = 1.5708
    c: Vertical(g7)
    c: Tangent(g7,g4) = 1.5708
    c: Horizontal(g8)
    c: Horizontal(g9)
    c: Vertical(g10)
    c: Horizontal(g11)
    c: Vertical(g12)
    c: Horizontal(g13)
    c: Vertical(g14)
    c: PointOnObject(g16,g10)
    c: PointOnObject(g16,g11)
    c: Tangent(g10,g15) = -1.5708
    c: Tangent(g11,g15) = -1.5708
    c: Tangent(g2,g4) = -1.5708
    c: Coincident(g0,g2)
    c: Tangent(g14,g17) = -1.5708
    c: Tangent(g17,g13) = -1.5708
    c: Equal(g17,g4)
    c: Equal(g4,g5)
    c: Tangent(g1,g5) = 1.5708
    c: Coincident(g1,g0)
    c: Equal(g17,g15)
    c: Radius(g4) = 1.2
    c: PointOnObject(g19,g1)
    c: PointOnObject(g19,g3)
    c: Tangent(g1,g18) = -1.5708
    c: Tangent(g3,g18) = 1.5708
    c: PointOnObject(g21,g2)
    c: PointOnObject(g21,g3)
    c: Tangent(g2,g20) = 1.5708
    c: Tangent(g3,g20) = 1.5708
    c: PointOnObject(g23,g7)
    c: PointOnObject(g23,g8)
    c: Tangent(g7,g22) = -1.5708
    c: Tangent(g8,g22) = -1.5708
    c: PointOnObject(g25,g8)
    c: PointOnObject(g25,g14)
    c: Tangent(g8,g24) = -1.5708
    c: Tangent(g14,g24) = 1.5708
    c: PointOnObject(g27,g12)
    c: PointOnObject(g27,g13)
    c: Tangent(g12,g26) = 1.5708
    c: Tangent(g13,g26) = 1.5708
    c: PointOnObject(g29,g11)
    c: PointOnObject(g29,g12)
    c: Tangent(g11,g28) = 1.5708
    c: Tangent(g12,g28) = 1.5708
    c: PointOnObject(g31,g9)
    c: PointOnObject(g31,g10)
    c: Tangent(g9,g30) = 1.5708
    c: Tangent(g10,g30) = 1.5708
    c: PointOnObject(g33,g6)
    c: PointOnObject(g33,g9)
    c: Tangent(g6,g32) = -1.5708
    c: Tangent(g9,g32) = 1.5708
    c: PointOnObject(g-4,g9)
    c: Equal(g32,g5)
    c: Equal(g5,g18)
    c: Equal(g18,g20)
    c: Equal(g4,g22)
    c: Equal(g22,g24)
    c: Equal(g17,g26)
    c: Equal(g26,g28)
    c: Equal(g30,g15)
    c: Equal(g11,g13)
    c: Equal(g14,g10)
    c: Equal(g13,g2)
    c: Equal(g6,g10)
    c: Equal(g14,g7)
    c: PointOnObject(g2,g-5)
    c: Tangent(g36,g40) = -1.5708
    c: Tangent(g36,g41) = -1.5708
    c: Tangent(g37,g41) = -1.5708
    c: Tangent(g37,g42) = -1.5708
    c: Tangent(g38,g42) = -1.5708
    c: Tangent(g38,g43) = -1.5708
    c: Tangent(g39,g43) = -1.5708
    c: Tangent(g39,g40) = -1.5708
    c: Vertical(g36)
    c: Vertical(g38)
    c: Horizontal(g37)
    c: Horizontal(g39)
    c: Equal(g40,g41)
    c: Equal(g41,g42)
    c: Equal(g42,g43)
    c: PointOnObject(g44,g36)
    c: PointOnObject(g44,g39)
    c: PointOnObject(g45,g37)
    c: PointOnObject(g45,g38)
    c: Equal(g40,g-15)
    c: Equal(g39,g-14)
    c: Equal(g36,g-8)
    c: Symmetric(g3,g3,g46)
    c: Coincident(g46,g34)
    c: Horizontal(g46)
    c: Coincident(g47,g34)
    c: Symmetric(g36,g36,g47)
    c: Horizontal(g47)
    c: Symmetric(g38,g38,g48)
    c: Coincident(g48,g35)
    c: Horizontal(g48)
    c: Equal(g46,g49)
    c: Coincident(g50,g-7)
    c: Symmetric(g-8,g-8,g50)
    c: Symmetric(g-12,g-12,g51)
    c: Coincident(g51,g-6)
    c: Equal(g51,g48)
    c: Equal(g47,g50)
    c: Coincident(g49,g35)
    c: Symmetric(g12,g12,g49)
    c: Diameter(g34) = 3
    c: Equal(g35,g34)
    c: Tangent(g52,g56) = -1.5708
    c: Tangent(g52,g57) = -1.5708
    c: Tangent(g53,g57) = -1.5708
    c: Tangent(g53,g58) = -1.5708
    c: Tangent(g54,g58) = -1.5708
    c: Tangent(g54,g59) = -1.5708
    c: Tangent(g55,g59) = -1.5708
    c: Tangent(g55,g56) = -1.5708
    c: Vertical(g52)
    c: Vertical(g54)
    c: Horizontal(g53)
    c: Horizontal(g55)
    c: Equal(g58,g59)
    c: PointOnObject(g60,g52)
    c: PointOnObject(g60,g55)
    c: PointOnObject(g61,g53)
    c: PointOnObject(g61,g54)
    c: Coincident(g58,g42)
    c: Coincident(g57,g41)
    c: Coincident(g56,g40)
    c: Distance(g55,g39) = 0.127
    c: Coincident(g62,g-16)
    c: Coincident(g62,g-1)
    c: Coincident(g63,g0)
    c: Coincident(g63,g13)
    c: Equal(g63,g62)
    c: Tangent(g64,g66) = 1.5708
    c: Tangent(g64,g67) = -1.5708
    c: Tangent(g65,g66) = 1.5708
    c: Tangent(g65,g67) = -1.5708
    c: Equal(g64,g65)
    c: Horizontal(g66)
    c: Tangent(g68,g70) = 1.5708
    c: Tangent(g68,g71) = -1.5708
    c: Tangent(g69,g70) = 1.5708
    c: Tangent(g69,g71) = -1.5708
    c: Equal(g68,g69)
    c: Horizontal(g70)
    c: Symmetric(g8,g8,g72)
    c: Symmetric(g71,g71,g72)
    c: Vertical(g72)
    c: Symmetric(g9,g9,g73)
    c: Symmetric(g66,g66,g73)
    c: Vertical(g73)
    c: Distance(g71,g70) = 2.1082
    c: Equal(g72,g73)
    c: Symmetric(g70,g70,g74)
    c: Coincident(g74,g72)
    c: Equal(g74,g72)
    c: PointOnObject(g75,g7)
    c: PointOnObject(g75,g68)
    c: Horizontal(g75)
    c: Equal(g75,g72)
    c: Equal(g64,g68)
    c: Equal(g67,g70)
    c: Perpendicular(g68,g75)
FEATURE [PartDesign::Pad] Pad
  Direction = (1,0,0)
  Length = 1.8542
  Length2 = 10
  Profile = -> Sketch
  ReferenceAxis = -> Sketch [N_Axis]
  Refine = true
  Suppressed = false
  Type = 0
  expr: Length = dimensions#VarSet.EnclosureTotalThickness
FEATURE [PartDesign::Body] Body  label="PsuSideShort"
  AllowCompound = false
  Group = -> [Binder,Binder001,Sketch,Pad]
  Origin = -> Origin
  Tip = -> Pad
COMPONENT P5 — same part as P4; its construction recipe is shown at P4.
COMPONENT P6 — recipe-attached ("PsuTopAndBottom", a linked part whose construction recipe lives in a companion FreeCAD document of the same project; that document's serialized recipe follows).
Construction recipe (the companion document, serialized — sketch geometry with constraints, then the solid features built on it; lengths are millimeters unless a unit is written):

FCSTD DOCUMENT  (FreeCAD 1.0R38641 +468 (Git))
Label: psu_top_and_bottom
License: All rights reserved
LicenseURL: https://en.wikipedia.org/wiki/All_rights_reserved
objects: PartDesign::SubShapeBinder×2, Sketcher::SketchObject×1, PartDesign::Pad×1, PartDesign::Body×1
note: 8 computed .brp shape members not serialized (recipe doc carries the construction recipe); baked Part::Feature solids carry a one-line shape summary decoded from their .brp
EXTERNAL_REF file=../panel_back.FCStd obj=Body
EXTERNAL_REF file=../../third_party/doepfer_psu3.FCStd obj=Sketch
EXTERNAL_REF file=../panel_back.FCStd obj=Sketch
EXTERNAL_REF file=../../third_party/doepfer_psu3.FCStd obj=Body
EXTERNAL_REF file=../dimensions.FCStd obj=VarSet

FEATURE [PartDesign::SubShapeBinder] Binder  label="PanelBackBinder"
  BindCopyOnChange = 0
  BindMode = 0
  ClaimChildren = false
  Context = -> Body [Binder.]
  Fuse = false
  MakeFace = true
  OffsetFill = false
  OffsetIntersection = false
  OffsetJoinType = 0
  OffsetOpenResult = false
  PartialLoad = false
  Refine = true
  Relative = true
  Support = -> [<external ../panel_back.FCStd>#Body]
  _Version = 2
FEATURE [PartDesign::SubShapeBinder] Binder001  label="Psu3Binder"
  BindCopyOnChange = 0
  BindMode = 0
  ClaimChildren = false
  Context = -> Body [Binder001.]
  Fuse = false
  MakeFace = true
  OffsetFill = false
  OffsetIntersection = false
  OffsetJoinType = 0
  OffsetOpenResult = false
  PartialLoad = false
  Placement = pos=(103,130,-16.25) rot=(1,0,0;-1.5708rad)
  Refine = true
  Relative = true
  Support = -> [<external ../../third_party/doepfer_psu3.FCStd>#Body]
  _Version = 2
  expr: .Placement.Base.x = (panel_back#Sketch.Constraints.DeltaX - panel_back#Sketch.Constraints.OffsetX - doepfer_psu3#Sketch.Constraints.Width) / 2 - 10 mm
  expr: .Placement.Base.z = (doepfer_psu3#Sketch.Constraints.Height - (panel_back#Sketch.Constraints.DeltaY - panel_back#Sketch.Constraints.OffsetY)) / 2
FEATURE [Sketcher::SketchObject] Sketch
  ArcFitTolerance = 1e-06
  AttachmentSupport = -> [Binder]
  ExternalGeometry = -> [Binder001,Binder]
  FullyConstrained = true
  MakeInternals = false
  MapMode = 5
  Placement = pos=(0,127.227,-5.85e-14) rot=(0,0.707107,0.707107;3.14159rad)
  expr: Constraints[113] = dimensions#VarSet.EnclosureFinishThickness
  expr: Constraints[36] = dimensions#VarSet.EnclosureTotalThickness + 2 * dimensions#VarSet.EnclosureFinishThickness
  sketch-geometry (95):
    g0: LineSegment StartX=-330.325 StartY=-11.1254 StartZ=0 EndX=-330.325 EndY=-101.375 EndZ=0
    g1: LineSegment StartX=-96.6754 StartY=-101.375 StartZ=0 EndX=-96.6754 EndY=-11.1254 EndZ=0
    g2: Circle CenterX=-320.25 CenterY=-2.0081 CenterZ=0 NormalX=0 NormalY=0 NormalZ=1 AngleXU=0 Radius=1.627
    g3: Circle CenterX=-106.75 CenterY=-2.0081 CenterZ=0 NormalX=0 NormalY=0 NormalZ=1 AngleXU=0 Radius=1.627
    g4: Circle CenterX=-122.1 CenterY=-36.55 CenterZ=0 NormalX=0 NormalY=0 NormalZ=1 AngleXU=0 Radius=1.5
    g5: Circle CenterX=-122.1 CenterY=-75.95 CenterZ=0 NormalX=0 NormalY=0 NormalZ=1 AngleXU=0 Radius=1.5
    g6: Circle CenterX=-106.75 CenterY=-110.492 CenterZ=0 NormalX=0 NormalY=0 NormalZ=1 AngleXU=0 Radius=1.627
    g7: Circle CenterX=-320.25 CenterY=-110.492 CenterZ=0 NormalX=0 NormalY=0 NormalZ=1 AngleXU=0 Radius=1.627
    g8: Circle CenterX=-274.5 CenterY=-91.15 CenterZ=0 NormalX=0 NormalY=0 NormalZ=1 AngleXU=0 Radius=1.5
    g9: Circle CenterX=-274.5 CenterY=-21.35 CenterZ=0 NormalX=0 NormalY=0 NormalZ=1 AngleXU=0 Radius=1.5
    g10: ArcOfCircle CenterX=-329.125 CenterY=-11.1254 CenterZ=0 NormalX=0 NormalY=0 NormalZ=1 AngleXU=0 Radius=1.2 StartAngle=1.5708 EndAngle=3.14159
    g11: GeomPoint [constr] X=-330.325 Y=-9.9254 Z=0
    g12: ArcOfCircle CenterX=-329.125 CenterY=-101.375 CenterZ=0 NormalX=0 NormalY=0 NormalZ=1 AngleXU=0 Radius=1.2 StartAngle=3.14159 EndAngle=4.71239
    g13: GeomPoint [constr] X=-330.325 Y=-102.575 Z=0
    g14: ArcOfCircle CenterX=-97.8754 CenterY=-101.375 CenterZ=0 NormalX=0 NormalY=0 NormalZ=1 AngleXU=0 Radius=1.2 StartAngle=4.71239 EndAngle=6.28319
    g15: GeomPoint [constr] X=-96.6754 Y=-102.575 Z=0
    g16: ArcOfCircle CenterX=-97.8754 CenterY=-11.1254 CenterZ=0 NormalX=0 NormalY=0 NormalZ=1 AngleXU=0 Radius=1.2 StartAngle=2e-16 EndAngle=1.5708
    g17: GeomPoint [constr] X=-96.6754 Y=-9.9254 Z=0
    g18: ArcOfCircle CenterX=-327.162 CenterY=-24.579 CenterZ=0 NormalX=0 NormalY=0 NormalZ=1 AngleXU=0 Radius=1.0541 StartAngle=-9e-16 EndAngle=3.14159
    g19: ArcOfCircle CenterX=-327.162 CenterY=-87.921 CenterZ=0 NormalX=0 NormalY=0 NormalZ=1 AngleXU=0 Radius=1.0541 StartAngle=3.14159 EndAngle=6.28319
    g20: LineSegment StartX=-326.108 StartY=-24.579 StartZ=0 EndX=-326.108 EndY=-87.921 EndZ=0
    g21: LineSegment StartX=-328.216 StartY=-24.579 StartZ=0 EndX=-328.216 EndY=-87.921 EndZ=0
    g22: LineSegment [constr] StartX=-330.325 StartY=-56.25 StartZ=0 EndX=-328.216 EndY=-56.25 EndZ=0
    g23: ArcOfCircle CenterX=-99.8377 CenterY=-24.579 CenterZ=0 NormalX=0 NormalY=0 NormalZ=1 AngleXU=0 Radius=1.0541 StartAngle=-9e-16 EndAngle=3.14159
    g24: ArcOfCircle CenterX=-99.8377 CenterY=-87.921 CenterZ=0 NormalX=0 NormalY=0 NormalZ=1 AngleXU=0 Radius=1.0541 StartAngle=3.14159 EndAngle=6.28319
    g25: LineSegment StartX=-98.7836 StartY=-24.579 StartZ=0 EndX=-98.7836 EndY=-87.921 EndZ=0
    g26: LineSegment StartX=-100.892 StartY=-24.579 StartZ=0 EndX=-100.892 EndY=-87.921 EndZ=0
    g27: LineSegment [constr] StartX=-98.7836 StartY=-56.25 StartZ=0 EndX=-96.6754 EndY=-56.25 EndZ=0
    g28: ArcOfCircle CenterX=-303.647 CenterY=-13.0877 CenterZ=0 NormalX=0 NormalY=0 NormalZ=1 AngleXU=0 Radius=1.0541 StartAngle=1.5708 EndAngle=4.71239
    g29: ArcOfCircle CenterX=-240.305 CenterY=-13.0877 CenterZ=0 NormalX=0 NormalY=0 NormalZ=1 AngleXU=0 Radius=1.0541 StartAngle=4.71239 EndAngle=7.85398
    g30: LineSegment StartX=-303.647 StartY=-12.0336 StartZ=0 EndX=-240.305 EndY=-12.0336 EndZ=0
    g31: LineSegment StartX=-303.647 StartY=-14.1418 StartZ=0 EndX=-240.305 EndY=-14.1418 EndZ=0
    g32: ArcOfCircle CenterX=-186.695 CenterY=-13.0877 CenterZ=0 NormalX=0 NormalY=0 NormalZ=1 AngleXU=0 Radius=1.0541 StartAngle=1.5708 EndAngle=4.71239
    g33: ArcOfCircle CenterX=-123.353 CenterY=-13.0877 CenterZ=0 NormalX=0 NormalY=0 NormalZ=1 AngleXU=0 Radius=1.0541 StartAngle=4.71239 EndAngle=7.85398
    g34: LineSegment StartX=-186.695 StartY=-12.0336 StartZ=0 EndX=-123.353 EndY=-12.0336 EndZ=0
    g35: LineSegment StartX=-186.695 StartY=-14.1418 StartZ=0 EndX=-123.353 EndY=-14.1418 EndZ=0
    g36: ArcOfCircle CenterX=-303.647 CenterY=-99.4123 CenterZ=0 NormalX=0 NormalY=0 NormalZ=1 AngleXU=0 Radius=1.0541 StartAngle=1.5708 EndAngle=4.71239
    g37: ArcOfCircle CenterX=-240.305 CenterY=-99.4123 CenterZ=0 NormalX=0 NormalY=0 NormalZ=1 AngleXU=0 Radius=1.0541 StartAngle=4.71239 EndAngle=7.85398
    g38: LineSegment StartX=-303.647 StartY=-98.3582 StartZ=0 EndX=-240.305 EndY=-98.3582 EndZ=0
    g39: LineSegment StartX=-303.647 StartY=-100.466 StartZ=0 EndX=-240.305 EndY=-100.466 EndZ=0
    g40: ArcOfCircle CenterX=-186.695 CenterY=-99.4123 CenterZ=0 NormalX=0 NormalY=0 NormalZ=1 AngleXU=0 Radius=1.0541 StartAngle=1.5708 EndAngle=4.71239
    g41: ArcOfCircle CenterX=-123.353 CenterY=-99.4123 CenterZ=0 NormalX=0 NormalY=0 NormalZ=1 AngleXU=0 Radius=1.0541 StartAngle=4.71239 EndAngle=7.85398
    g42: LineSegment StartX=-186.695 StartY=-98.3582 StartZ=0 EndX=-123.353 EndY=-98.3582 EndZ=0
    g43: LineSegment StartX=-186.695 StartY=-100.466 StartZ=0 EndX=-123.353 EndY=-100.466 EndZ=0
    g44: LineSegment [constr] StartX=-271.976 StartY=-100.466 StartZ=0 EndX=-271.976 EndY=-102.575 EndZ=0
    g45: LineSegment [constr] StartX=-155.024 StartY=-100.466 StartZ=0 EndX=-155.024 EndY=-102.575 EndZ=0
    g46: LineSegment [constr] StartX=-155.024 StartY=-12.0336 StartZ=0 EndX=-155.024 EndY=-9.9254 EndZ=0
    g47: LineSegment [constr] StartX=-271.976 StartY=-12.0336 StartZ=0 EndX=-271.976 EndY=-9.9254 EndZ=0
    g48: LineSegment [constr] StartX=-271.976 StartY=-98.3582 StartZ=0 EndX=-271.976 EndY=-14.1418 EndZ=0
    g49: LineSegment [constr] StartX=-155.024 StartY=-14.1418 StartZ=0 EndX=-155.024 EndY=-98.3582 EndZ=0
    g50: LineSegment [constr] StartX=-257.002 StartY=2.8729 StartZ=0 EndX=-257.002 EndY=-9.9254 EndZ=0
    g51: LineSegment [constr] StartX=-257.002 StartY=-115.373 StartZ=0 EndX=-257.002 EndY=-102.575 EndZ=0
    g52: LineSegment [constr] StartX=-328.216 StartY=-56.25 StartZ=0 EndX=-326.108 EndY=-56.25 EndZ=0
    g53: LineSegment [constr] StartX=-213.5 StartY=-9.9254 StartZ=0 EndX=-213.5 EndY=-102.575 EndZ=0
    g54: LineSegment [constr] StartX=-213.627 StartY=-9.9254 StartZ=0 EndX=-213.627 EndY=-102.575 EndZ=0
    g55: LineSegment [constr] StartX=-330.325 StartY=-98.3582 StartZ=0 EndX=-271.976 EndY=-98.3582 EndZ=0
    g56: LineSegment [constr] StartX=-271.976 StartY=-98.3582 StartZ=0 EndX=-213.627 EndY=-98.3582 EndZ=0
    g57: LineSegment [constr] StartX=-155.024 StartY=-98.3582 StartZ=0 EndX=-96.6754 EndY=-98.3582 EndZ=0
    g58: LineSegment [constr] StartX=-240.305 StartY=-14.1418 StartZ=0 EndX=-240.305 EndY=-16.25 EndZ=0
    g59: LineSegment [constr] StartX=-103 StartY=-56.25 StartZ=0 EndX=-100.892 EndY=-56.25 EndZ=0
    g60: ArcOfCircle CenterX=-320.25 CenterY=-2.0081 CenterZ=0 NormalX=0 NormalY=0 NormalZ=1 AngleXU=0 Radius=3.7352 StartAngle=0 EndAngle=3.14159
    g61: LineSegment StartX=-316.515 StartY=-2.0081 StartZ=0 EndX=-316.515 EndY=-8.7254 EndZ=0
    g62: LineSegment StartX=-325.185 StartY=-9.9254 StartZ=0 EndX=-329.125 EndY=-9.9254 EndZ=0
    g63: LineSegment StartX=-329.125 StartY=-102.575 StartZ=0 EndX=-325.185 EndY=-102.575 EndZ=0
    g64: LineSegment StartX=-315.315 StartY=-102.575 StartZ=0 EndX=-111.685 EndY=-102.575 EndZ=0
    g65: LineSegment StartX=-101.815 StartY=-102.575 StartZ=0 EndX=-97.8754 EndY=-102.575 EndZ=0
    g66: LineSegment StartX=-111.685 StartY=-9.9254 StartZ=0 EndX=-315.315 EndY=-9.9254 EndZ=0
    g67: LineSegment StartX=-97.8754 StartY=-9.9254 StartZ=0 EndX=-101.815 EndY=-9.9254 EndZ=0
    g68: ArcOfCircle CenterX=-320.25 CenterY=-110.492 CenterZ=0 NormalX=0 NormalY=0 NormalZ=1 AngleXU=0 Radius=3.7352 StartAngle=3.14159 EndAngle=6.28319
    g69: ArcOfCircle CenterX=-106.75 CenterY=-110.492 CenterZ=0 NormalX=0 NormalY=0 NormalZ=1 AngleXU=0 Radius=3.7352 StartAngle=3.14159 EndAngle=6.28319
    g70: ArcOfCircle CenterX=-106.75 CenterY=-2.0081 CenterZ=0 NormalX=0 NormalY=0 NormalZ=1 AngleXU=0 Radius=3.7352 StartAngle=0 EndAngle=3.14159
    g71: LineSegment StartX=-323.985 StartY=-2.0081 StartZ=0 EndX=-323.985 EndY=-8.7254 EndZ=0
    g72: LineSegment StartX=-323.985 StartY=-110.492 StartZ=0 EndX=-323.985 EndY=-103.775 EndZ=0
    g73: LineSegment StartX=-316.515 StartY=-110.492 StartZ=0 EndX=-316.515 EndY=-103.775 EndZ=0
    g74: LineSegment StartX=-110.485 StartY=-110.492 StartZ=0 EndX=-110.485 EndY=-103.775 EndZ=0
    g75: LineSegment StartX=-103.015 StartY=-110.492 StartZ=0 EndX=-103.015 EndY=-103.775 EndZ=0
    g76: LineSegment StartX=-110.485 StartY=-2.0081 StartZ=0 EndX=-110.485 EndY=-8.7254 EndZ=0
    g77: LineSegment StartX=-103.015 StartY=-2.0081 StartZ=0 EndX=-103.015 EndY=-8.7254 EndZ=0
    g78: LineSegment [constr] StartX=-318.623 StartY=-110.492 StartZ=0 EndX=-316.515 EndY=-110.492 EndZ=0
    g79: ArcOfCircle CenterX=-325.185 CenterY=-8.7254 CenterZ=0 NormalX=0 NormalY=0 NormalZ=1 AngleXU=0 Radius=1.2 StartAngle=4.71239 EndAngle=6.28319
    g80: GeomPoint [constr] X=-323.985 Y=-9.9254 Z=0
    g81: ArcOfCircle CenterX=-315.315 CenterY=-8.7254 CenterZ=0 NormalX=0 NormalY=0 NormalZ=1 AngleXU=0 Radius=1.2 StartAngle=3.14159 EndAngle=4.71239
    g82: GeomPoint [constr] X=-316.515 Y=-9.9254 Z=0
    g83: ArcOfCircle CenterX=-111.685 CenterY=-8.7254 CenterZ=0 NormalX=0 NormalY=0 NormalZ=1 AngleXU=0 Radius=1.2 StartAngle=4.71239 EndAngle=6.28319
    g84: GeomPoint [constr] X=-110.485 Y=-9.9254 Z=0
    g85: ArcOfCircle CenterX=-101.815 CenterY=-8.7254 CenterZ=0 NormalX=0 NormalY=0 NormalZ=1 AngleXU=0 Radius=1.2 StartAngle=3.14159 EndAngle=4.71239
    g86: GeomPoint [constr] X=-103.015 Y=-9.9254 Z=0
    g87: ArcOfCircle CenterX=-111.685 CenterY=-103.775 CenterZ=0 NormalX=0 NormalY=0 NormalZ=1 AngleXU=0 Radius=1.2 StartAngle=4.8e-15 EndAngle=1.5708
    g88: GeomPoint [constr] X=-110.485 Y=-102.575 Z=0
    g89: ArcOfCircle CenterX=-101.815 CenterY=-103.775 CenterZ=0 NormalX=0 NormalY=0 NormalZ=1 AngleXU=0 Radius=1.2 StartAngle=1.5708 EndAngle=3.14159
    g90: GeomPoint [constr] X=-103.015 Y=-102.575 Z=0
    g91: ArcOfCircle CenterX=-325.185 CenterY=-103.775 CenterZ=0 NormalX=0 NormalY=0 NormalZ=1 AngleXU=0 Radius=1.2 StartAngle=3.3e-15 EndAngle=1.5708
    g92: GeomPoint [constr] X=-323.985 Y=-102.575 Z=0
    g93: ArcOfCircle CenterX=-315.315 CenterY=-103.775 CenterZ=0 NormalX=0 NormalY=0 NormalZ=1 AngleXU=0 Radius=1.2 StartAngle=1.5708 EndAngle=3.14159
    g94: GeomPoint [constr] X=-316.515 Y=-102.575 Z=0
  constraints (223):
    c: Vertical(g1)
    c: Coincident(g2,g-7)
    c: Equal(g2,g-7)
    c: Coincident(g3,g-10)
    c: Equal(g3,g-10)
    c: Coincident(g4,g-4)
    c: Equal(g4,g-4)
    c: Coincident(g5,g-5)
    c: Equal(g5,g-5)
    c: Coincident(g6,g-9)
    c: Equal(g6,g-9)
    c: Coincident(g7,g-8)
    c: Equal(g7,g-8)
    c: Coincident(g8,g-6)
    c: Equal(g8,g-6)
    c: Coincident(g9,g-3)
    c: Equal(g9,g-3)
    c: PointOnObject(g11,g0)
    c: Tangent(g0,g10) = -1.5708
    c: PointOnObject(g13,g0)
    c: Tangent(g0,g12) = -1.5708
    c: PointOnObject(g15,g1)
    c: Tangent(g1,g14) = -1.5708
    c: PointOnObject(g17,g1)
    c: Tangent(g1,g16) = -1.5708
    c: Equal(g-11,g10)
    c: Equal(g10,g12)
    c: Equal(g12,g14)
    c: Equal(g14,g16)
    c: Tangent(g18,g20) = 1.5708
    c: Tangent(g18,g21) = -1.5708
    c: Tangent(g19,g20) = 1.5708
    c: Tangent(g19,g21) = -1.5708
    c: Equal(g18,g19)
    c: Vertical(g20)
    c: Equal(g21,g-14)
    c: Distance(g20,g21) = 2.1082
    c: Symmetric(g0,g0,g22)
    c: Symmetric(g21,g21,g22)
    c: Horizontal(g22)
    c: Tangent(g23,g25) = 1.5708
    c: Tangent(g23,g26) = -1.5708
    c: Tangent(g24,g25) = 1.5708
    c: Tangent(g24,g26) = -1.5708
    c: Equal(g23,g24)
    c: Vertical(g26)
    c: Equal(g26,g21)
    c: Equal(g23,g18)
    c: Symmetric(g25,g25,g27)
    c: Symmetric(g1,g1,g27)
    c: Horizontal(g27)
    c: Equal(g27,g22)
    c: Tangent(g28,g30) = 1.5708
    c: Tangent(g28,g31) = -1.5708
    c: Tangent(g29,g30) = 1.5708
    c: Tangent(g29,g31) = -1.5708
    c: Equal(g28,g29)
    c: Horizontal(g30)
    c: Tangent(g32,g34) = 1.5708
    c: Tangent(g32,g35) = -1.5708
    c: Tangent(g33,g34) = 1.5708
    c: Tangent(g33,g35) = -1.5708
    c: Equal(g32,g33)
    c: Horizontal(g34)
    c: Equal(g29,g32)
    c: Equal(g18,g28)
    c: Tangent(g36,g38) = 1.5708
    c: Tangent(g36,g39) = -1.5708
    c: Tangent(g37,g38) = 1.5708
    c: Tangent(g37,g39) = -1.5708
    c: Equal(g36,g37)
    c: Horizontal(g38)
    c: Tangent(g40,g42) = 1.5708
    c: Tangent(g40,g43) = -1.5708
    c: Tangent(g41,g42) = 1.5708
    c: Tangent(g41,g43) = -1.5708
    c: Equal(g40,g41)
    c: Horizontal(g42)
    c: Equal(g41,g24)
    c: Equal(g40,g37)
    c: Symmetric(g39,g39,g44)
    c: Vertical(g44)
    c: Symmetric(g43,g43,g45)
    c: Vertical(g45)
    c: Symmetric(g34,g34,g46)
    c: Vertical(g46)
    c: Symmetric(g30,g30,g47)
    c: Vertical(g47)
    c: Symmetric(g38,g38,g48)
    c: Symmetric(g31,g31,g48)
    c: Vertical(g48)
    c: Equal(g44,g22)
    c: Equal(g22,g47)
    c: Equal(g47,g46)
    c: Equal(g45,g46)
    c: Symmetric(g35,g35,g49)
    c: Symmetric(g42,g42,g49)
    c: Vertical(g49)
    c: Equal(g42,g38)
    c: Equal(g38,g31)
    c: Equal(g35,g42)
    c: Equal(g31,g20)
    c: Symmetric(g-15,g-15,g50)
    c: Vertical(g50)
    c: PointOnObject(g51,g-12)
    c: Equal(g51,g50)
    c: Tangent(g51,g50)
    c: Coincident(g52,g22)
    c: Symmetric(g20,g20,g52)
    c: Equal(g52,g22)
    c: Symmetric(g67,g62,g53)
    c: Symmetric(g63,g65,g53)
    c: Vertical(g54)
    c: Distance(g53,g54) = 0.127
    c: PointOnObject(g55,g0)
    c: Horizontal(g55)
    c: Coincident(g56,g55)
    c: PointOnObject(g56,g54)
    c: Horizontal(g56)
    c: Equal(g55,g56)
    c: PointOnObject(g57,g1)
    c: Horizontal(g57)
    c: Equal(g57,g55)
    c: Coincident(g55,g48)
    c: Coincident(g57,g49)
    c: Coincident(g58,g29)
    c: PointOnObject(g58,g-16)
    c: Vertical(g58)
    c: Equal(g47,g58)
    c: Symmetric(g-17,g-17,g59)
    c: Symmetric(g26,g26,g59)
    c: Equal(g59,g27)
    c: Vertical(g0)
    c: Coincident(g60,g2)
    c: Vertical(g61)
    c: Horizontal(g62)
    c: Horizontal(g63)
    c: PointOnObject(g13,g63)
    c: PointOnObject(g15,g63)
    c: PointOnObject(g44,g63)
    c: PointOnObject(g45,g63)
    c: PointOnObject(g51,g63)
    c: PointOnObject(g54,g63)
    c: PointOnObject(g11,g67)
    c: PointOnObject(g17,g67)
    c: PointOnObject(g46,g67)
    c: PointOnObject(g47,g67)
    c: PointOnObject(g50,g67)
    c: PointOnObject(g54,g67)
    c: Coincident(g68,g7)
    c: Coincident(g69,g6)
    c: Coincident(g70,g3)
    c: Vertical(g71)
    c: Vertical(g72)
    c: Vertical(g73)
    c: Vertical(g74)
    c: Vertical(g75)
    c: Vertical(g76)
    c: Vertical(g77)
    c: Tangent(g76,g70) = -1.5708
    c: Tangent(g77,g70) = 1.5708
    c: Tangent(g61,g60) = 1.5708
    c: Tangent(g71,g60) = -1.5708
    c: Tangent(g68,g73) = -1.5708
    c: Tangent(g72,g68) = 1.5708
    c: Tangent(g69,g74) = 1.5708
    c: Tangent(g69,g75) = -1.5708
    c: Tangent(g65,g64)
    c: Tangent(g64,g63)
    c: Tangent(g62,g66)
    c: Tangent(g67,g66)
    c: Equal(g68,g60)
    c: Equal(g60,g70)
    c: Equal(g70,g69)
    c: Tangent(g12,g63) = -1.5708
    c: Tangent(g10,g62) = -1.5708
    c: Tangent(g16,g67) = -1.5708
    c: Tangent(g14,g65) = -1.5708
    c: PointOnObject(g78,g7)
    c: Coincident(g78,g68)
    c: Horizontal(g78)
    c: Equal(g78,g44)
    c: PointOnObject(g80,g62)
    c: PointOnObject(g80,g71)
    c: Tangent(g62,g79) = 1.5708
    c: Tangent(g71,g79) = 1.5708
    c: PointOnObject(g82,g61)
    c: PointOnObject(g82,g66)
    c: Tangent(g61,g81) = -1.5708
    c: Tangent(g66,g81) = 1.5708
    c: Equal(g79,g10)
    c: Equal(g79,g81)
    c: PointOnObject(g84,g66)
    c: PointOnObject(g84,g76)
    c: Tangent(g66,g83) = 1.5708
    c: Tangent(g76,g83) = 1.5708
    c: PointOnObject(g86,g67)
    c: PointOnObject(g86,g77)
    c: Tangent(g67,g85) = 1.5708
    c: Tangent(g77,g85) = -1.5708
    c: Equal(g83,g85)
    c: Equal(g85,g16)
    c: PointOnObject(g88,g64)
    c: PointOnObject(g88,g74)
    c: Tangent(g64,g87) = 1.5708
    c: Tangent(g74,g87) = -1.5708
    c: PointOnObject(g90,g65)
    c: PointOnObject(g90,g75)
    c: Tangent(g65,g89) = 1.5708
    c: Tangent(g75,g89) = 1.5708
    c: Equal(g89,g14)
    c: Equal(g87,g89)
    c: PointOnObject(g92,g63)
    c: PointOnObject(g92,g72)
    c: Tangent(g63,g91) = 1.5708
    c: Tangent(g72,g91) = -1.5708
    c: PointOnObject(g94,g64)
    c: PointOnObject(g94,g73)
    c: Tangent(g64,g93) = 1.5708
    c: Tangent(g73,g93) = 1.5708
    c: Equal(g93,g91)
    c: Equal(g91,g12)
    c: Equal(g63,g65)
FEATURE [PartDesign::Pad] Pad
  Direction = (0,1,-2e-16)
  Length = 1.8542
  Length2 = 10
  Profile = -> Sketch
  ReferenceAxis = -> Sketch [N_Axis]
  Refine = true
  Suppressed = false
  Type = 0
  expr: Length = dimensions#VarSet.EnclosureTotalThickness
FEATURE [PartDesign::Body] Body  label="PsuTopAndBottom"
  AllowCompound = false
  Group = -> [Binder,Binder001,Sketch,Pad]
  Origin = -> Origin
  Tip = -> Pad
COMPONENT P7 — same part as P6; its construction recipe is shown at P6.
PROVENANCE & LICENSES
A FreeCAD (.FCStd) document from a public repository crawl; recipes are the document's own serialized feature recipes (and, for linked parts, companion documents' recipes).
License: cc-by-sa-4.0.
